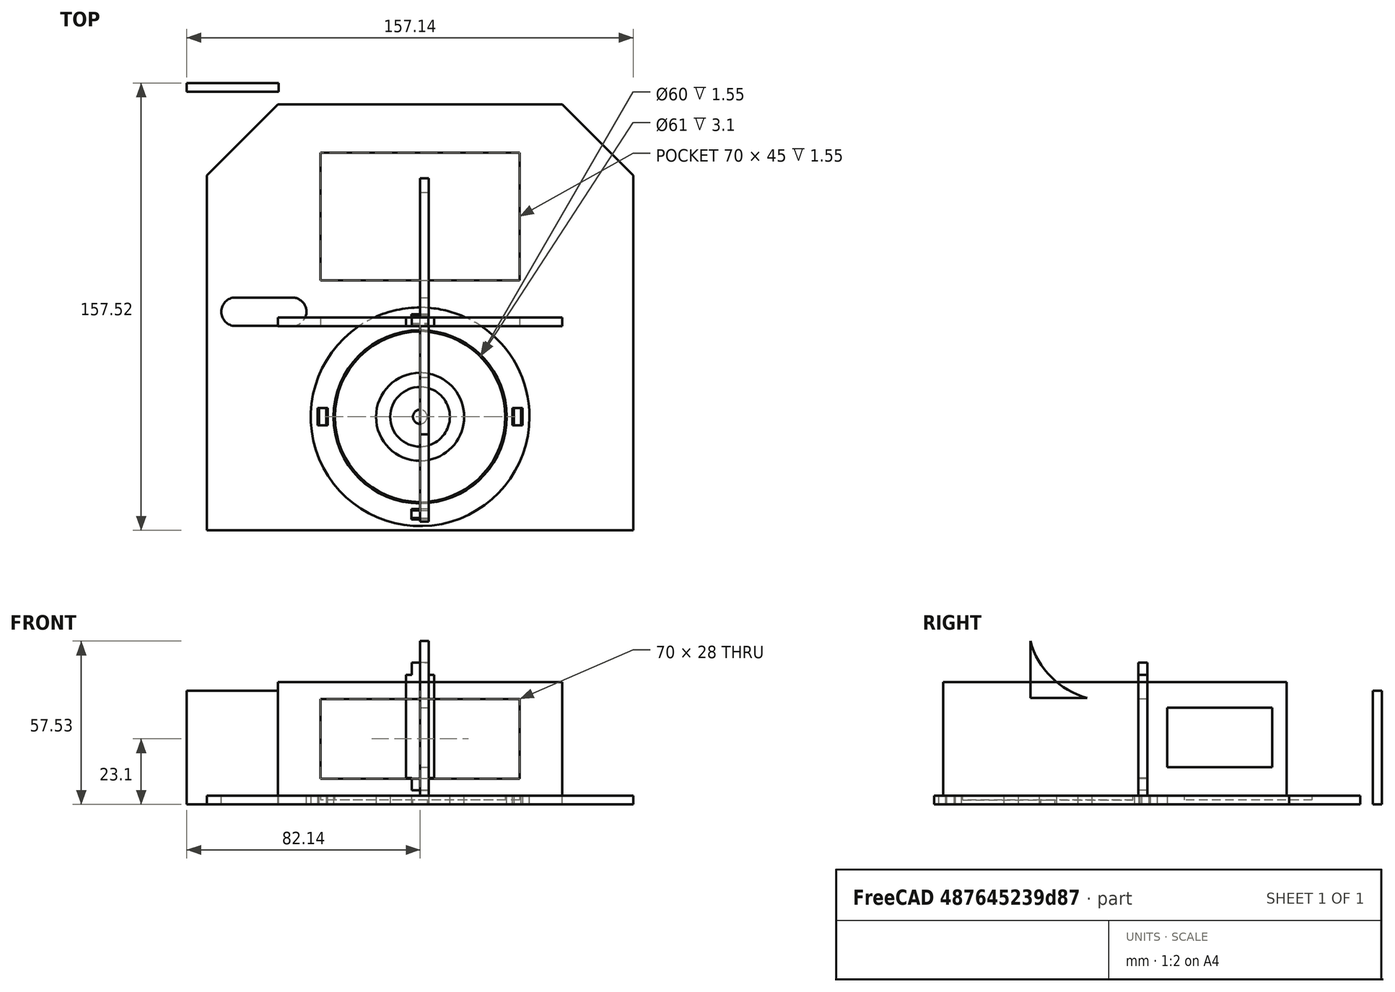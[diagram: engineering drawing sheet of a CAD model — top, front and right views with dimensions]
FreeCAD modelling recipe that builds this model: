
FCSTD DOCUMENT  (FreeCAD 1.0R39109 (Git))
Label: Vehicle_project_3
License: All rights reserved
LicenseURL: https://en.wikipedia.org/wiki/All_rights_reserved
objects: Sketcher::SketchObject×29, PartDesign::Pocket×17, App::Link×15, App::FeaturePython×15, PartDesign::Pad×12, PartDesign::Body×12, Part::Part2DObjectPython×12, Part::FeaturePython×3, PartDesign::Fillet×2, PartDesign::Mirrored×2, App::DocumentObjectGroup×2, App::VarSet×1, Part::Plane×1, App::Part×1, Assembly::JointGroup×1, Assembly::AssemblyObject×1
note: 183 computed .brp shape members not serialized (recipe doc carries the construction recipe); baked Part::Feature solids carry a one-line shape summary decoded from their .brp

FEATURE [App::VarSet] VarSet  label="dimensions"
  base_height = 40
  base_length = 150
  base_short_side = 25
  base_width = 150
  board_length = 50
  board_width = 80
  bridge_side = 45
  hole_margin = 1
  material_thickness = 3.1
  raspberry_length = 61
  raspberry_width = 89
FEATURE [Sketcher::SketchObject] Sketch
  ArcFitTolerance = 1e-06
  AttachmentSupport = -> [XY_Plane]
  FullyConstrained = true
  MakeInternals = false
  MapMode = 5
  expr: Constraints[11] = <<dimensions>>.base_width
  expr: Constraints[12] = <<dimensions>>.base_length
  expr: Constraints[14] = <<dimensions>>.base_length / 2
  expr: Constraints[15] = <<dimensions>>.base_short_side
  expr: Constraints[16] = <<dimensions>>.base_short_side
  sketch-geometry (6):
    g0: LineSegment StartX=-75 StartY=50 StartZ=0 EndX=-75 EndY=-75 EndZ=0
    g1: LineSegment StartX=-75 StartY=-75 StartZ=0 EndX=75 EndY=-75 EndZ=0
    g2: LineSegment StartX=75 StartY=-75 StartZ=0 EndX=75 EndY=50 EndZ=0
    g3: LineSegment StartX=75 StartY=50 StartZ=0 EndX=50 EndY=75 EndZ=0
    g4: LineSegment StartX=50 StartY=75 StartZ=0 EndX=-50 EndY=75 EndZ=0
    g5: LineSegment StartX=-50 StartY=75 StartZ=0 EndX=-75 EndY=50 EndZ=0
  constraints (17):
    c: Vertical(g0)
    c: Coincident(g0,g1)
    c: Horizontal(g1)
    c: Coincident(g1,g2)
    c: Vertical(g2)
    c: Coincident(g2,g3)
    c: Coincident(g3,g4)
    c: Horizontal(g4)
    c: Coincident(g4,g5)
    c: Coincident(g5,g0)
    c: Equal(g5,g3)
    c: DistanceX(g1,g1) = 150
    c: Distance(g1,g4) = 150
    c: Symmetric(g0,g2,g-2)
    c: Distance(g-1,g1) = 75
    c: DistanceY(g0,g4) = 25
    c: DistanceX(g0,g4) = 25
FEATURE [PartDesign::Pad] Pad
  Direction = (0,0,1)
  Length = 3.1
  Length2 = 10
  Profile = -> Sketch
  ReferenceAxis = -> Sketch [N_Axis]
  Refine = true
  Suppressed = false
  Type = 0
  expr: Length = <<dimensions>>.material_thickness
FEATURE [Sketcher::SketchObject] Sketch001
  ArcFitTolerance = 1e-06
  AttachmentSupport = -> [Pad]
  ExternalGeometry = -> [Pad]
  FullyConstrained = true
  MakeInternals = false
  MapMode = 5
  Placement = pos=(0,0,3.1) rot=(0,0,1;0rad)
  expr: Constraints[10] = <<dimensions>>.material_thickness + <<dimensions>>.hole_margin
  expr: Constraints[11] = <<dimensions>>.material_thickness + <<dimensions>>.hole_margin
  expr: Constraints[8] = <<dimensions>>.raspberry_width
  expr: Constraints[9] = <<dimensions>>.raspberry_length
  sketch-geometry (4):
    g0: LineSegment StartX=-70.9 StartY=-9.9 StartZ=0 EndX=-70.9 EndY=-70.9 EndZ=0
    g1: LineSegment StartX=-70.9 StartY=-70.9 StartZ=0 EndX=18.1 EndY=-70.9 EndZ=0
    g2: LineSegment StartX=18.1 StartY=-70.9 StartZ=0 EndX=18.1 EndY=-9.9 EndZ=0
    g3: LineSegment StartX=18.1 StartY=-9.9 StartZ=0 EndX=-70.9 EndY=-9.9 EndZ=0
  constraints (12):
    c: Vertical(g0)
    c: Coincident(g0,g1)
    c: Coincident(g1,g2)
    c: Coincident(g2,g3)
    c: Coincident(g3,g0)
    c: Horizontal(g0,g2)
    c: Horizontal(g1,g0)
    c: Vertical(g2)
    c: DistanceX(g3,g3) = 89
    c: DistanceY(g2,g2) = 61
    c: Distance(g-3,g0) = 4.1
    c: Distance(g1,g-4) = 4.1
FEATURE [PartDesign::Pocket] Pocket
  BaseFeature = -> Pad
  Direction = (0,0,-1)
  Length = 1.55
  Length2 = 5
  Profile = -> Sketch001
  ReferenceAxis = -> Sketch001 [N_Axis]
  Refine = true
  Suppressed = false
  Type = 0
  expr: Length = <<dimensions>>.material_thickness / 2
FEATURE [Sketcher::SketchObject] Sketch002
  ArcFitTolerance = 1e-06
  AttachmentSupport = -> [Pocket]
  ExternalGeometry = -> [Pocket]
  FullyConstrained = true
  MakeInternals = false
  MapMode = 5
  Placement = pos=(0,0,3.1) rot=(0,0,1;0rad)
  sketch-geometry (4):
    g0: LineSegment StartX=-70.9 StartY=46.8875 StartZ=0 EndX=-70.9 EndY=-3.11249 EndZ=0
    g1: LineSegment StartX=-70.9 StartY=-3.11249 StartZ=0 EndX=9.1 EndY=-3.11249 EndZ=0
    g2: LineSegment StartX=9.1 StartY=-3.11249 StartZ=0 EndX=9.1 EndY=46.8875 EndZ=0
    g3: LineSegment StartX=9.1 StartY=46.8875 StartZ=0 EndX=-70.9 EndY=46.8875 EndZ=0
  constraints (12):
    c: Coincident(g0,g1)
    c: Coincident(g1,g2)
    c: Coincident(g2,g3)
    c: Coincident(g3,g0)
    c: Horizontal(g3)
    c: Horizontal(g1)
    c: Vertical(g2)
    c: Vertical(g0)
    c: DistanceX(g3,g3) = 80  '=di'
    c: DistanceY(g0,g0) = 50
    c: Vertical(g0,g-4)
    c: Distance(g0,g-6) = 5.1
FEATURE [PartDesign::Pocket] Pocket001
  BaseFeature = -> Pocket
  Direction = (0,0,-1)
  Length = 1.55
  Length2 = 5
  Profile = -> Sketch002
  ReferenceAxis = -> Sketch002 [N_Axis]
  Refine = true
  Suppressed = false
  Type = 0
  expr: Length = <<dimensions>>.material_thickness / 2
FEATURE [Sketcher::SketchObject] Sketch003
  ArcFitTolerance = 1e-06
  AttachmentSupport = -> [Pocket001]
  ExternalGeometry = -> [Pocket001]
  FullyConstrained = true
  MakeInternals = false
  MapMode = 5
  Placement = pos=(0,0,3.1) rot=(0,0,1;0rad)
  expr: Constraints[9] = <<dimensions>>.material_thickness + 3 mm
  sketch-geometry (4):
    g0: LineSegment StartX=45 StartY=-61.9 StartZ=0 EndX=45 EndY=-68.9 EndZ=0
    g1: LineSegment StartX=45 StartY=-68.9 StartZ=0 EndX=60 EndY=-68.9 EndZ=0
    g2: LineSegment StartX=60 StartY=-68.9 StartZ=0 EndX=60 EndY=-61.9 EndZ=0
    g3: LineSegment StartX=60 StartY=-61.9 StartZ=0 EndX=45 EndY=-61.9 EndZ=0
  constraints (12):
    c: Coincident(g0,g1)
    c: Coincident(g1,g2)
    c: Coincident(g2,g3)
    c: Coincident(g3,g0)
    c: Horizontal(g3)
    c: Horizontal(g1)
    c: Vertical(g0)
    c: Vertical(g2)
    c: Distance(g-3,g2) = 15
    c: Distance(g-4,g1) = 6.1
    c: DistanceY(g2,g2) = 7
    c: DistanceX(g3,g3) = 15
FEATURE [PartDesign::Pocket] Pocket002
  BaseFeature = -> Pocket001
  Direction = (0,0,-1)
  Length = 5
  Length2 = 5
  Profile = -> Sketch003
  ReferenceAxis = -> Sketch003 [N_Axis]
  Refine = true
  Suppressed = false
  Type = 1
FEATURE [PartDesign::Fillet] Fillet
  Base = -> Pocket002 [Edge36,Edge38,Edge35,Edge37]
  BaseFeature = -> Pocket002
  Radius = 3
  Refine = true
  SupportTransform = false
  Suppressed = false
  UseAllEdges = false
FEATURE [Sketcher::SketchObject] Sketch004
  ArcFitTolerance = 1e-06
  AttachmentSupport = -> [Fillet]
  ExternalGeometry = -> [Fillet]
  FullyConstrained = true
  MakeInternals = false
  MapMode = 5
  Placement = pos=(0,0,3.1) rot=(0,0,1;0rad)
  expr: Constraints[8] = <<dimensions>>.bridge_side
  expr: Constraints[9] = <<dimensions>>.bridge_side
  sketch-geometry (4):
    g0: LineSegment StartX=19.1 StartY=46.8875 StartZ=0 EndX=19.1 EndY=1.88751 EndZ=0
    g1: LineSegment StartX=19.1 StartY=1.88751 StartZ=0 EndX=64.1 EndY=1.88751 EndZ=0
    g2: LineSegment StartX=64.1 StartY=1.88751 StartZ=0 EndX=64.1 EndY=46.8875 EndZ=0
    g3: LineSegment StartX=64.1 StartY=46.8875 StartZ=0 EndX=19.1 EndY=46.8875 EndZ=0
  constraints (12):
    c: Vertical(g0)
    c: Coincident(g0,g1)
    c: Coincident(g1,g2)
    c: Coincident(g2,g3)
    c: Coincident(g3,g0)
    c: Horizontal(g3)
    c: Vertical(g2)
    c: Horizontal(g1)
    c: DistanceY(g2,g2) = 45
    c: DistanceX(g3,g3) = 45
    c: Distance(g-3,g0) = 10
    c: Horizontal(g-3,g0)
FEATURE [PartDesign::Pocket] Pocket003
  BaseFeature = -> Fillet
  Direction = (0,0,-1)
  Length = 1.55
  Length2 = 5
  Profile = -> Sketch004
  ReferenceAxis = -> Sketch004 [N_Axis]
  Refine = true
  Suppressed = false
  Type = 0
  expr: Length = <<dimensions>>.material_thickness / 2
FEATURE [Sketcher::SketchObject] Sketch005
  ArcFitTolerance = 1e-06
  AttachmentSupport = -> [XZ_Plane001]
  FullyConstrained = true
  MakeInternals = false
  MapMode = 5
  Placement = pos=(0,0,0) rot=(1,0,0;1.5708rad)
  expr: Constraints[10] = <<dimensions>>.material_thickness
  expr: Constraints[7] = <<dimensions>>.base_width
  expr: Constraints[8] = <<dimensions>>.base_height
  sketch-geometry (4):
    g0: LineSegment StartX=-75 StartY=43.1 StartZ=0 EndX=-75 EndY=3.1 EndZ=0
    g1: LineSegment StartX=-75 StartY=3.1 StartZ=0 EndX=75 EndY=3.1 EndZ=0
    g2: LineSegment StartX=75 StartY=3.1 StartZ=0 EndX=75 EndY=43.1 EndZ=0
    g3: LineSegment StartX=75 StartY=43.1 StartZ=0 EndX=-75 EndY=43.1 EndZ=0
  constraints (11):
    c: Vertical(g0)
    c: Coincident(g0,g1)
    c: Horizontal(g1)
    c: Coincident(g1,g2)
    c: Coincident(g2,g3)
    c: Coincident(g3,g0)
    c: Vertical(g2)
    c: DistanceX(g3,g3) = 150
    c: DistanceY(g2,g2) = 40
    c: Symmetric(g0,g2,g-2)
    c: Distance(g-1,g1) = 3.1
FEATURE [PartDesign::Pad] Pad001
  Direction = (0,-1,2e-16)
  Length = 3.1
  Length2 = 10
  Placement = pos=(0,0,0) rot=(1,0,0;1.5708rad)
  Profile = -> Sketch005
  ReferenceAxis = -> Sketch005 [N_Axis]
  Refine = true
  Suppressed = false
  Type = 0
  expr: Length = <<dimensions>>.material_thickness
FEATURE [Sketcher::SketchObject] Sketch006
  ArcFitTolerance = 1e-06
  AttachmentSupport = -> [Pad001]
  ExternalGeometry = -> [Pad001]
  FullyConstrained = true
  MakeInternals = false
  MapMode = 5
  Placement = pos=(0,-3.1,0) rot=(1,0,0;1.5708rad)
  expr: Constraints[8] = <<dimensions>>.material_thickness + 5 mm
  sketch-geometry (4):
    g0: LineSegment StartX=-66.9 StartY=18.1 StartZ=0 EndX=-66.9 EndY=6.1 EndZ=0
    g1: LineSegment StartX=-66.9 StartY=6.1 StartZ=0 EndX=-51.9 EndY=6.1 EndZ=0
    g2: LineSegment StartX=-51.9 StartY=6.1 StartZ=0 EndX=-51.9 EndY=18.1 EndZ=0
    g3: LineSegment StartX=-51.9 StartY=18.1 StartZ=0 EndX=-66.9 EndY=18.1 EndZ=0
  constraints (12):
    c: Coincident(g0,g1)
    c: Horizontal(g1)
    c: Coincident(g1,g2)
    c: Coincident(g2,g3)
    c: Coincident(g3,g0)
    c: Horizontal(g3)
    c: Vertical(g2)
    c: Vertical(g0)
    c: Distance(g-3,g0) = 8.1
    c: Distance(g-4,g1) = 3
    c: DistanceY(g0,g0) = 12
    c: DistanceX(g1,g1) = 15
FEATURE [PartDesign::Pocket] Pocket004
  BaseFeature = -> Pad001
  Direction = (0,1,-2e-16)
  Length = 5
  Length2 = 5
  Placement = pos=(0,0,0) rot=(1,0,0;1.5708rad)
  Profile = -> Sketch006
  ReferenceAxis = -> Sketch006 [N_Axis]
  Refine = true
  Suppressed = false
  Type = 1
FEATURE [PartDesign::Fillet] Fillet001
  Base = -> Pocket004 [Edge23,Edge22,Edge21,Edge24]
  BaseFeature = -> Pocket004
  Placement = pos=(0,0,0) rot=(1,0,0;1.5708rad)
  Radius = 2
  Refine = true
  SupportTransform = false
  Suppressed = false
  UseAllEdges = false
FEATURE [PartDesign::Body] Body001  label="back_side"
  AllowCompound = false
  Group = -> [Sketch005,Pad001,Sketch006,Pocket004,Fillet001]
  Origin = -> Origin001
  Tip = -> Fillet001
FEATURE [Sketcher::SketchObject] Sketch007
  ArcFitTolerance = 1e-06
  AttachmentSupport = -> [YZ_Plane002]
  FullyConstrained = true
  MakeInternals = false
  MapMode = 5
  Placement = pos=(0,0,0) rot=(0.57735,0.57735,0.57735;2.0944rad)
  expr: Constraints[10] = <<dimensions>>.base_length / 2 - <<dimensions>>.material_thickness
  expr: Constraints[11] = <<dimensions>>.material_thickness
  expr: Constraints[8] = <<dimensions>>.base_height
  expr: Constraints[9] = <<dimensions>>.base_length - <<dimensions>>.material_thickness - 26 mm
  sketch-geometry (4):
    g0: LineSegment StartX=-71.9 StartY=43.1 StartZ=0 EndX=-71.9 EndY=3.1 EndZ=0
    g1: LineSegment StartX=-71.9 StartY=3.1 StartZ=0 EndX=49 EndY=3.1 EndZ=0
    g2: LineSegment StartX=-71.9 StartY=43.1 StartZ=0 EndX=49 EndY=43.1 EndZ=0
    g3: LineSegment StartX=49 StartY=43.1 StartZ=0 EndX=49 EndY=3.1 EndZ=0
  constraints (12):
    c: Coincident(g0,g1)
    c: Horizontal(g1)
    c: Coincident(g0,g2)
    c: Coincident(g2,g3)
    c: Coincident(g3,g1)
    c: Vertical(g3)
    c: Horizontal(g2)
    c: Vertical(g0)
    c: DistanceY(g0,g0) = 40
    c: DistanceX(g1,g1) = 120.9
    c: Distance(g-2,g0) = 71.9
    c: Distance(g-1,g1) = 3.1
FEATURE [PartDesign::Pad] Pad002
  Direction = (1,0,0)
  Length = 3.1
  Length2 = 10
  Placement = pos=(0,0,0) rot=(1,1,1;2.0944rad)
  Profile = -> Sketch007
  ReferenceAxis = -> Sketch007 [N_Axis]
  Refine = true
  Suppressed = false
  Type = 0
  expr: Length = <<dimensions>>.material_thickness
FEATURE [PartDesign::Body] Body002  label="right_side"
  AllowCompound = false
  Group = -> [Sketch007,Pad002]
  Origin = -> Origin002
  Tip = -> Pad002
FEATURE [Sketcher::SketchObject] Sketch008
  ArcFitTolerance = 1e-06
  AttachmentSupport = -> [YZ_Plane003]
  FullyConstrained = true
  MakeInternals = false
  MapMode = 5
  Placement = pos=(0,0,0) rot=(0.57735,0.57735,0.57735;2.0944rad)
  sketch-geometry (4):
    g0: LineSegment StartX=-71.9 StartY=43.1 StartZ=0 EndX=-71.9 EndY=3.1 EndZ=0
    g1: LineSegment StartX=-71.9 StartY=3.1 StartZ=0 EndX=49 EndY=3.1 EndZ=0
    g2: LineSegment StartX=-71.9 StartY=43.1 StartZ=0 EndX=49 EndY=43.1 EndZ=0
    g3: LineSegment StartX=49 StartY=43.1 StartZ=0 EndX=49 EndY=3.1 EndZ=0
  constraints (12):
    c: Coincident(g0,g1)
    c: Horizontal(g1)
    c: Coincident(g0,g2)
    c: Coincident(g2,g3)
    c: Coincident(g3,g1)
    c: Vertical(g3)
    c: Horizontal(g2)
    c: Vertical(g0)
    c: DistanceY(g0,g0) = 40
    c: DistanceX(g1,g1) = 120.9
    c: Distance(g-2,g0) = 71.9
    c: Distance(g-1,g1) = 3.1
FEATURE [PartDesign::Pad] Pad003
  Direction = (1,0,0)
  Length = 3.1
  Length2 = 10
  Placement = pos=(0,0,0) rot=(1,1,1;2.0944rad)
  Profile = -> Sketch008
  ReferenceAxis = -> Sketch008 [N_Axis]
  Refine = true
  Suppressed = false
  Type = 0
  expr: Length = <<dimensions>>.material_thickness
FEATURE [Sketcher::SketchObject] Sketch009
  ArcFitTolerance = 1e-06
  AttachmentSupport = -> [Pad003]
  ExternalGeometry = -> [Pad003]
  FullyConstrained = true
  MakeInternals = false
  MapMode = 5
  Placement = pos=(0,0,0) rot=(0.57735,0.57735,-0.57735;4.18879rad)
  sketch-geometry (4):
    g0: LineSegment StartX=44 StartY=-34.1 StartZ=0 EndX=44 EndY=-13.1 EndZ=0
    g1: LineSegment StartX=44 StartY=-13.1 StartZ=0 EndX=7 EndY=-13.1 EndZ=0
    g2: LineSegment StartX=7 StartY=-13.1 StartZ=0 EndX=7 EndY=-34.1 EndZ=0
    g3: LineSegment StartX=7 StartY=-34.1 StartZ=0 EndX=44 EndY=-34.1 EndZ=0
  constraints (12):
    c: Coincident(g0,g1)
    c: Horizontal(g1)
    c: Coincident(g1,g2)
    c: Coincident(g2,g3)
    c: Coincident(g3,g0)
    c: Horizontal(g3)
    c: Vertical(g0)
    c: Vertical(g2)
    c: Distance(g-4,g0) = 5
    c: Distance(g-3,g3) = 9
    c: DistanceY(g0,g0) = 21
    c: DistanceX(g1,g1) = 37
FEATURE [PartDesign::Pocket] Pocket005
  BaseFeature = -> Pad003
  Direction = (1,0,0)
  Length = 5
  Length2 = 5
  Placement = pos=(0,0,0) rot=(1,1,1;2.0944rad)
  Profile = -> Sketch009
  ReferenceAxis = -> Sketch009 [N_Axis]
  Refine = true
  Suppressed = false
  Type = 1
FEATURE [PartDesign::Body] Body003  label="left_side"
  AllowCompound = false
  Group = -> [Sketch008,Pad003,Sketch009,Pocket005]
  Origin = -> Origin003
  Tip = -> Pocket005
FEATURE [Sketcher::SketchObject] Sketch010
  ArcFitTolerance = 1e-06
  AttachmentSupport = -> [XY_Plane004]
  FullyConstrained = false
  MakeInternals = false
  MapMode = 5
  expr: Constraints[8] = sqrt(1250) - 3
  expr: Constraints[9] = <<dimensions>>.material_thickness
  sketch-geometry (4):
    g0: LineSegment StartX=-82.1409 StartY=82.5247 StartZ=0 EndX=-49.7856 EndY=82.5247 EndZ=0
    g1: LineSegment StartX=-49.7856 StartY=82.5247 StartZ=0 EndX=-49.7856 EndY=79.4247 EndZ=0
    g2: LineSegment StartX=-49.7856 StartY=79.4247 StartZ=0 EndX=-82.1409 EndY=79.4247 EndZ=0
    g3: LineSegment StartX=-82.1409 StartY=79.4247 StartZ=0 EndX=-82.1409 EndY=82.5247 EndZ=0
  constraints (10):
    c: Horizontal(g0)
    c: Coincident(g0,g1)
    c: Coincident(g1,g2)
    c: Horizontal(g2)
    c: Coincident(g2,g3)
    c: Coincident(g3,g0)
    c: Vertical(g3)
    c: Vertical(g1)
    c: DistanceX(g0,g0) = 32.3553
    c: DistanceY(g1,g1) = 3.1
FEATURE [PartDesign::Pad] Pad004
  Direction = (0,0,1)
  Length = 40
  Length2 = 10
  Profile = -> Sketch010
  ReferenceAxis = -> Sketch010 [N_Axis]
  Refine = true
  Suppressed = false
  Type = 0
  expr: Length = <<dimensions>>.base_height
FEATURE [PartDesign::Body] Body004  label="front_angle_side"
  AllowCompound = false
  Group = -> [Sketch010,Pad004]
  Origin = -> Origin004
  Tip = -> Pad004
FEATURE [Sketcher::SketchObject] Sketch011
  ArcFitTolerance = 1e-06
  AttachmentSupport = -> [XZ_Plane005]
  FullyConstrained = true
  MakeInternals = false
  MapMode = 5
  Placement = pos=(0,0,0) rot=(1,0,0;1.5708rad)
  expr: Constraints[15] = <<dimensions>>.base_width / 2 - 25 mm
  expr: Constraints[18] = <<dimensions>>.material_thickness
  expr: Constraints[23] = <<dimensions>>.base_height
  sketch-geometry (8):
    g0: LineSegment StartX=0 StartY=43.1 StartZ=0 EndX=0 EndY=37.1 EndZ=0
    g1: LineSegment StartX=-35 StartY=37.1 StartZ=0 EndX=-35 EndY=9.1 EndZ=0
    g2: LineSegment StartX=-35 StartY=9.1 StartZ=0 EndX=0 EndY=9.1 EndZ=0
    g3: LineSegment StartX=0 StartY=9.1 StartZ=0 EndX=0 EndY=3.1 EndZ=0
    g4: LineSegment StartX=0 StartY=3.1 StartZ=0 EndX=-50 EndY=3.1 EndZ=0
    g5: LineSegment StartX=-50 StartY=3.1 StartZ=0 EndX=-50 EndY=43.1 EndZ=0
    g6: LineSegment StartX=-50 StartY=43.1 StartZ=0 EndX=0 EndY=43.1 EndZ=0
    g7: LineSegment StartX=0 StartY=37.1 StartZ=0 EndX=-35 EndY=37.1 EndZ=0
  constraints (24):
    c: PointOnObject(g0,g-2)
    c: PointOnObject(g0,g-2)
    c: Vertical(g1)
    c: Coincident(g1,g2)
    c: PointOnObject(g2,g-2)
    c: Horizontal(g2)
    c: Coincident(g2,g3)
    c: PointOnObject(g3,g-2)
    c: Coincident(g3,g4)
    c: Horizontal(g4)
    c: Coincident(g4,g5)
    c: Vertical(g5)
    c: Coincident(g5,g6)
    c: Coincident(g6,g0)
    c: Horizontal(g6)
    c: DistanceX(g4,g4) = 50
    c: Distance(g4,g2) = 6
    c: Distance(g5,g1) = 15
    c: Distance(g-1,g4) = 3.1
    c: Coincident(g0,g7)
    c: Coincident(g7,g1)
    c: Horizontal(g7)
    c: Distance(g6,g7) = 6
    c: DistanceY(g5,g5) = 40
FEATURE [PartDesign::Pad] Pad005
  Direction = (0,-1,2e-16)
  Length = 3.1
  Length2 = 10
  Placement = pos=(0,0,0) rot=(1,0,0;1.5708rad)
  Profile = -> Sketch011
  ReferenceAxis = -> Sketch011 [N_Axis]
  Refine = true
  Suppressed = false
  Type = 0
  expr: Length = <<dimensions>>.material_thickness
FEATURE [PartDesign::Mirrored] Mirrored
  BaseFeature = -> Pad005
  MirrorPlane = -> YZ_Plane005
  Placement = pos=(0,0,0) rot=(1,0,0;1.5708rad)
  Refine = true
  Suppressed = false
  TransformMode = 1
FEATURE [PartDesign::Body] Body005  label="front_side"
  AllowCompound = false
  Group = -> [Sketch011,Pad005,Mirrored]
  Origin = -> Origin005
  Tip = -> Mirrored
FEATURE [App::Link] base  label="base001"
  LinkedObject = -> Body
FEATURE [App::FeaturePython] GroundedJoint  # Assembly grounded joint (typed FeaturePython)
  ObjectToGround = -> base
FEATURE [App::Link] back_side  label="back_side001"
  LinkPlacement = pos=(-3e-15,-71.9,-1e-15) rot=(0,0,1;0rad)
  LinkedObject = -> Body001
  Placement = pos=(-3e-15,-71.9,-1e-15) rot=(0,0,1;0rad)
FEATURE [App::FeaturePython] Joint  label="Fixed"  # Assembly joint (typed FeaturePython)
  Activated = true
  AngleMax = 0
  AngleMin = 0
  Detach1 = false
  Detach2 = false
  Distance = 0
  Distance2 = 0
  EnableAngleMax = false
  EnableAngleMin = false
  EnableLengthMax = false
  EnableLengthMin = false
  JointType = 0 (Fixed)
  LengthMax = 0
  LengthMin = 0
  Placement1 = pos=(3e-15,-3.1,3.1) rot=(0.707107,0,0.707107;3.14159rad)
  Placement2 = pos=(0,-75,3.1) rot=(0.707107,0,0.707107;3.14159rad)
  Reference1 = -> Assembly [back_side.Edge35,back_side.Edge35]
  Reference2 = -> Assembly [base.Edge37,base.Edge37]
FEATURE [App::Link] left_side  label="left_side001"
  LinkPlacement = pos=(-75,-3.57e-14,3.6e-14) rot=(0,0,1;0rad)
  LinkedObject = -> Body003
  Placement = pos=(-75,-3.57e-14,3.6e-14) rot=(0,0,1;0rad)
FEATURE [App::Link] right_side  label="right_side001"
  LinkPlacement = pos=(71.9,-1.35e-14,1.91e-14) rot=(0,0,1;0rad)
  LinkedObject = -> Body002
  Placement = pos=(71.9,-1.35e-14,1.91e-14) rot=(0,0,1;0rad)
FEATURE [App::FeaturePython] Joint001  label="Fixed001"  # Assembly joint (typed FeaturePython)
  Activated = true
  AngleMax = 0
  AngleMin = 0
  Detach1 = false
  Detach2 = false
  Distance = 0
  Distance2 = 0
  EnableAngleMax = false
  EnableAngleMin = false
  EnableLengthMax = false
  EnableLengthMin = false
  JointType = 0 (Fixed)
  LengthMax = 0
  LengthMin = 0
  Offset2 = pos=(0,0,1) rot=(0,0,1;3.14159rad)
  Placement1 = pos=(0,49,3.1) rot=(0.57735,0.57735,0.57735;4.18879rad)
  Placement2 = pos=(-75,49,3.1) rot=(-0.57735,0.57735,-0.57735;4.18879rad)
  Reference1 = -> Assembly [left_side.Edge9,left_side.Vertex7]
  Reference2 = -> Assembly [base.Edge33,base.Vertex23]
FEATURE [App::FeaturePython] Joint002  label="Fixed002"  # Assembly joint (typed FeaturePython)
  Activated = true
  AngleMax = 0
  AngleMin = 0
  Detach1 = false
  Detach2 = false
  Distance = 0
  Distance2 = 0
  EnableAngleMax = false
  EnableAngleMin = false
  EnableLengthMax = false
  EnableLengthMin = false
  JointType = 0 (Fixed)
  LengthMax = 0
  LengthMin = 0
  Offset2 = pos=(0,0,-1) rot=(0,0,1;0rad)
  Placement1 = pos=(3.1,49,3.1) rot=(0.57735,0.57735,0.57735;4.18879rad)
  Placement2 = pos=(75,49,3.1) rot=(0.57735,0.57735,0.57735;4.18879rad)
  Reference1 = -> Assembly [right_side.Edge7,right_side.Vertex6]
  Reference2 = -> Assembly [base.Edge41,base.Vertex28]
FEATURE [App::Link] front_angle_side  label="front_angle_side001"
  LinkPlacement = pos=(50.7893,-42.4969,3.1) rot=(0,0,-1;0.785398rad)
  LinkedObject = -> Body004
  Placement = pos=(50.7893,-42.4969,3.1) rot=(0,0,-1;0.785398rad)
FEATURE [App::Link] front_angle_side001  label="front_angle_side002"
  LinkPlacement = pos=(43.0783,51.3707,3.1) rot=(0,0,1;0.785398rad)
  LinkedObject = -> Body004
  Placement = pos=(43.0783,51.3707,3.1) rot=(0,0,1;0.785398rad)
FEATURE [App::FeaturePython] Joint003  label="Fixed003"  # Assembly joint (typed FeaturePython)
  Activated = true
  AngleMax = 0
  AngleMin = 0
  Detach1 = false
  Detach2 = false
  Distance = 0
  Distance2 = 0
  EnableAngleMax = false
  EnableAngleMin = false
  EnableLengthMax = false
  EnableLengthMin = false
  JointType = 0 (Fixed)
  LengthMax = 0
  LengthMin = 0
  Offset2 = pos=(0,0,0) rot=(0,0,-1;1.5708rad)
  Placement1 = pos=(-65.9632,82.5247,0) rot=(0.707107,0,0.707107;3.14159rad)
  Placement2 = pos=(62.5,62.5,3.1) rot=(-0.357407,-0.862856,-0.357407;1.71777rad)
  Reference1 = -> Assembly [front_angle_side.Edge3,front_angle_side.Edge3]
  Reference2 = -> Assembly [base.Edge42,base.Edge42]
FEATURE [App::FeaturePython] Joint004  label="Fixed004"  # Assembly joint (typed FeaturePython)
  Activated = true
  AngleMax = 0
  AngleMin = 0
  Detach1 = false
  Detach2 = false
  Distance = 0
  Distance2 = 0
  EnableAngleMax = false
  EnableAngleMin = false
  EnableLengthMax = false
  EnableLengthMin = false
  JointType = 0 (Fixed)
  LengthMax = 0
  LengthMin = 0
  Offset2 = pos=(0,0,-17) rot=(0,0,-1;1.5708rad)
  Placement1 = pos=(-49.7856,82.5247,0) rot=(0.707107,0,0.707107;3.14159rad)
  Placement2 = pos=(-50.4792,74.5208,3.1) rot=(0.357407,-0.862856,0.357407;1.71777rad)
  Reference1 = -> Assembly [front_angle_side001.Edge3,front_angle_side001.Vertex3]
  Reference2 = -> Assembly [base.Edge35,base.Edge35]
FEATURE [App::Link] front_side  label="front_side001"
  LinkPlacement = pos=(2.7e-15,75,-5.4e-15) rot=(0,0,1;0rad)
  LinkedObject = -> Body005
  Placement = pos=(2.7e-15,75,-5.4e-15) rot=(0,0,1;0rad)
FEATURE [App::FeaturePython] Joint005  label="Fixed005"  # Assembly joint (typed FeaturePython)
  Activated = true
  AngleMax = 0
  AngleMin = 0
  Detach1 = false
  Detach2 = false
  Distance = 0
  Distance2 = 0
  EnableAngleMax = false
  EnableAngleMin = false
  EnableLengthMax = false
  EnableLengthMin = false
  JointType = 0 (Fixed)
  LengthMax = 0
  LengthMin = 0
  Offset2 = pos=(0,0,0) rot=(0,0,1;3.14159rad)
  Placement1 = pos=(-2.7e-15,0,3.1) rot=(0.707107,0,0.707107;3.14159rad)
  Placement2 = pos=(0,75,3.1) rot=(0,1,0;4.71239rad)
  Reference1 = -> Assembly [front_side.Edge7,front_side.Edge7]
  Reference2 = -> Assembly [base.Edge39,base.Edge39]
FEATURE [Sketcher::SketchObject] Sketch012
  ArcFitTolerance = 1e-06
  AttachmentSupport = -> [XY_Plane007]
  FullyConstrained = true
  MakeInternals = false
  MapMode = 5
  expr: Constraints[11] = <<dimensions>>.base_width
  expr: Constraints[12] = <<dimensions>>.base_length
  expr: Constraints[14] = <<dimensions>>.base_length / 2
  sketch-geometry (6):
    g0: LineSegment StartX=-75 StartY=50 StartZ=0 EndX=-75 EndY=-75 EndZ=0
    g1: LineSegment StartX=-75 StartY=-75 StartZ=0 EndX=75 EndY=-75 EndZ=0
    g2: LineSegment StartX=75 StartY=-75 StartZ=0 EndX=75 EndY=50 EndZ=0
    g3: LineSegment StartX=75 StartY=50 StartZ=0 EndX=50 EndY=75 EndZ=0
    g4: LineSegment StartX=50 StartY=75 StartZ=0 EndX=-50 EndY=75 EndZ=0
    g5: LineSegment StartX=-50 StartY=75 StartZ=0 EndX=-75 EndY=50 EndZ=0
  constraints (17):
    c: Vertical(g0)
    c: Coincident(g0,g1)
    c: Horizontal(g1)
    c: Coincident(g1,g2)
    c: Vertical(g2)
    c: Coincident(g2,g3)
    c: Coincident(g3,g4)
    c: Horizontal(g4)
    c: Coincident(g4,g5)
    c: Coincident(g5,g0)
    c: Equal(g5,g3)
    c: DistanceX(g1,g1) = 150
    c: Distance(g1,g4) = 150
    c: Symmetric(g0,g2,g-2)
    c: Distance(g-1,g1) = 75
    c: DistanceY(g0,g4) = 25
    c: DistanceX(g0,g4) = 25
FEATURE [PartDesign::Pad] Pad006
  Direction = (0,0,1)
  Length = 3.1
  Length2 = 10
  Profile = -> Sketch012
  ReferenceAxis = -> Sketch012 [N_Axis]
  Refine = true
  Suppressed = false
  Type = 0
  expr: Length = <<dimensions>>.material_thickness
FEATURE [App::FeaturePython] Joint007  label="Fixed006"  # Assembly joint (typed FeaturePython)
  Activated = true
  AngleMax = 0
  AngleMin = 0
  Detach1 = false
  Detach2 = false
  Distance = 0
  Distance2 = 0
  EnableAngleMax = false
  EnableAngleMin = false
  EnableLengthMax = false
  EnableLengthMin = false
  JointType = 0 (Fixed)
  LengthMax = 0
  LengthMin = 0
  Offset2 = pos=(0,0,-3) rot=(0,0,1;3.14159rad)
  Placement1 = pos=(-75,-75,0) rot=(-0.57735,-0.57735,0.57735;4.18879rad)
  Placement2 = pos=(-2.84e-14,-74.9,43.1) rot=(0.57735,-0.57735,-0.57735;4.18879rad)
  Reference1 = -> Assembly [top.Edge3,top.Vertex3]
  Reference2 = -> Assembly [left_side.Edge6,left_side.Vertex1]
FEATURE [Sketcher::SketchObject] Sketch013
  ArcFitTolerance = 1e-06
  AttachmentSupport = -> [Pad006]
  ExternalGeometry = -> [Pad006]
  FullyConstrained = true
  MakeInternals = false
  MapMode = 5
  Placement = pos=(0,0,3.1) rot=(0,0,1;0rad)
  sketch-geometry (1):
    g0: Circle CenterX=0 CenterY=-35 CenterZ=0 NormalX=0 NormalY=0 NormalZ=1 AngleXU=0 Radius=30
  constraints (3):
    c: PointOnObject(g0,g-2)
    c: Diameter(g0) = 60
    c: Distance(g0,g-3) = 40
FEATURE [PartDesign::Pocket] Pocket006
  BaseFeature = -> Pad006
  Direction = (0,0,-1)
  Length = 1.55
  Length2 = 5
  Profile = -> Sketch013
  ReferenceAxis = -> Sketch013 [N_Axis]
  Refine = true
  Suppressed = false
  Type = 0
  expr: Length = <<dimensions>>.material_thickness / 2
FEATURE [Sketcher::SketchObject] Sketch014
  ArcFitTolerance = 1e-06
  AttachmentSupport = -> [Pocket006]
  ExternalGeometry = -> [Pocket006]
  FullyConstrained = true
  MakeInternals = false
  MapMode = 5
  Placement = pos=(0,0,1.55) rot=(0,0,1;0rad)
  sketch-geometry (1):
    g0: Circle CenterX=0 CenterY=-35 CenterZ=0 NormalX=0 NormalY=0 NormalZ=1 AngleXU=0 Radius=2.5
  constraints (2):
    c: Coincident(g0,g-3)
    c: Diameter(g0) = 5
FEATURE [PartDesign::Pocket] Pocket007
  BaseFeature = -> Pocket006
  Direction = (0,0,-1)
  Length = 5
  Length2 = 5
  Profile = -> Sketch014
  ReferenceAxis = -> Sketch014 [N_Axis]
  Refine = true
  Suppressed = false
  Type = 1
FEATURE [Sketcher::SketchObject] Sketch016
  ArcFitTolerance = 1e-06
  FullyConstrained = false
  MakeInternals = false
  MapMode = 5
  Placement = pos=(0,0,3.1) rot=(0,0,1;0rad)
  expr: Constraints[11] = <<dimensions>>.material_thickness + 3 mm
  expr: Constraints[36] = <<dimensions>>.material_thickness + 3 mm
  expr: Constraints[37] = <<dimensions>>.material_thickness
  expr: Constraints[42] = <<dimensions>>.material_thickness
  expr: Constraints[43] = <<dimensions>>.material_thickness
  expr: Constraints[44] = <<dimensions>>.material_thickness + 3 mm
  expr: Constraints[47] = <<dimensions>>.material_thickness + 3 mm
  expr: Constraints[8] = <<dimensions>>.material_thickness
  sketch-geometry (18):
    g0: LineSegment StartX=-36.1 StartY=-31.95 StartZ=0 EndX=-33 EndY=-31.95 EndZ=0
    g1: LineSegment StartX=-33 StartY=-31.95 StartZ=0 EndX=-33 EndY=-38.05 EndZ=0
    g2: LineSegment StartX=-33 StartY=-38.05 StartZ=0 EndX=-36.1 EndY=-38.05 EndZ=0
    g3: LineSegment StartX=-36.1 StartY=-38.05 StartZ=0 EndX=-36.1 EndY=-31.95 EndZ=0
    g4: LineSegment [constr] StartX=0 StartY=-35 StartZ=0 EndX=-63.8249 EndY=-35 EndZ=0
    g5: LineSegment [constr] StartX=0 StartY=-35 StartZ=0 EndX=57.2559 EndY=-35 EndZ=0
    g6: LineSegment StartX=-3.05 StartY=-2 StartZ=0 EndX=3.05 EndY=-2 EndZ=0
    g7: LineSegment StartX=3.05 StartY=-2 StartZ=0 EndX=3.05 EndY=1.1 EndZ=0
    g8: LineSegment StartX=3.05 StartY=1.1 StartZ=0 EndX=-3.05 EndY=1.1 EndZ=0
    g9: LineSegment StartX=-3.05 StartY=1.1 StartZ=0 EndX=-3.05 EndY=-2 EndZ=0
    g10: LineSegment StartX=33 StartY=-31.95 StartZ=0 EndX=33 EndY=-38.05 EndZ=0
    g11: LineSegment StartX=33 StartY=-38.05 StartZ=0 EndX=36.1 EndY=-38.05 EndZ=0
    g12: LineSegment StartX=36.1 StartY=-38.05 StartZ=0 EndX=36.1 EndY=-31.95 EndZ=0
    g13: LineSegment StartX=36.1 StartY=-31.95 StartZ=0 EndX=33 EndY=-31.95 EndZ=0
    g14: LineSegment StartX=-3.05 StartY=-68 StartZ=0 EndX=3.05 EndY=-68 EndZ=0
    g15: LineSegment StartX=3.05 StartY=-68 StartZ=0 EndX=3.05 EndY=-71.1 EndZ=0
    g16: LineSegment StartX=3.05 StartY=-71.1 StartZ=0 EndX=-3.05 EndY=-71.1 EndZ=0
    g17: LineSegment StartX=-3.05 StartY=-71.1 StartZ=0 EndX=-3.05 EndY=-68 EndZ=0
  constraints (48):
    c: Horizontal(g0)
    c: Coincident(g0,g1)
    c: Coincident(g1,g2)
    c: Coincident(g2,g3)
    c: Coincident(g3,g0)
    c: Vertical(g1)
    c: Horizontal(g2)
    c: Vertical(g3)
    c: DistanceX(g0,g0) = 3.1
    c: Coincident(g4,g-3)
    c: Symmetric(g0,g1,g4)
    c: DistanceY(g3,g3) = 6.1
    c: Coincident(g5,g4)
    c: Horizontal(g5)
    c: Distance(g-3,g1) = 3
    c: Coincident(g6,g7)
    c: Coincident(g7,g8)
    c: Coincident(g8,g9)
    c: Coincident(g9,g6)
    c: Coincident(g10,g11)
    c: Horizontal(g11)
    c: Coincident(g11,g12)
    c: Coincident(g12,g13)
    c: Coincident(g13,g10)
    c: Horizontal(g14)
    c: Coincident(g14,g15)
    c: Coincident(g15,g16)
    c: Coincident(g16,g17)
    c: Coincident(g17,g14)
    c: Vertical(g7)
    c: Vertical(g9)
    c: Horizontal(g6)
    c: Horizontal(g13)
    c: Vertical(g10)
    c: Vertical(g15)
    c: Vertical(g17)
    c: DistanceY(g12,g12) = 6.1
    c: DistanceX(g13,g13) = 3.1
    c: Symmetric(g12,g11,g5)
    c: Distance(g-3,g10) = 3
    c: Symmetric(g15,g16,g-2)
    c: Symmetric(g7,g8,g-2)
    c: Distance(g15,g15) = 3.1
    c: DistanceY(g7,g7) = 3.1
    c: DistanceX(g16,g16) = 6.1
    c: Distance(g-3,g14) = 3
    c: Distance(g-3,g6) = 3
    c: DistanceX(g8,g8) = 6.1
FEATURE [PartDesign::Pocket] Pocket008
  BaseFeature = -> Pocket007
  Direction = (0,0,-1)
  Length = 5
  Length2 = 5
  Profile = -> Sketch016
  ReferenceAxis = -> Sketch016 [N_Axis]
  Refine = true
  Suppressed = false
  Type = 1
FEATURE [Sketcher::SketchObject] Sketch017
  ArcFitTolerance = 1e-06
  AttachmentSupport = -> [XZ_Plane008]
  FullyConstrained = true
  MakeInternals = false
  MapMode = 5
  Placement = pos=(0,0,0) rot=(1,0,0;1.5708rad)
  expr: Constraints[19] = (<<dimensions>>.material_thickness + 3 mm) / 2 * 0.95
  sketch-geometry (8):
    g0: LineSegment StartX=0 StartY=5 StartZ=0 EndX=2.8975 EndY=5 EndZ=0
    g1: LineSegment StartX=2.8975 StartY=5 StartZ=0 EndX=2.8975 EndY=9.33 EndZ=0
    g2: LineSegment StartX=2.8975 StartY=9.33 StartZ=0 EndX=5 EndY=9.33 EndZ=0
    g3: LineSegment StartX=5 StartY=9.33 StartZ=0 EndX=5 EndY=45.67 EndZ=0
    g4: LineSegment StartX=5 StartY=45.67 StartZ=0 EndX=2.8975 EndY=45.67 EndZ=0
    g5: LineSegment StartX=2.8975 StartY=45.67 StartZ=0 EndX=2.8975 EndY=50 EndZ=0
    g6: LineSegment StartX=2.8975 StartY=50 StartZ=0 EndX=0 EndY=50 EndZ=0
    g7: LineSegment StartX=0 StartY=50 StartZ=0 EndX=0 EndY=5 EndZ=0
  constraints (24):
    c: PointOnObject(g0,g-2)
    c: Horizontal(g0)
    c: Coincident(g0,g1)
    c: Vertical(g1)
    c: Coincident(g1,g2)
    c: Horizontal(g2)
    c: Coincident(g2,g3)
    c: Vertical(g3)
    c: Coincident(g3,g4)
    c: Horizontal(g4)
    c: Coincident(g4,g5)
    c: Vertical(g5)
    c: Coincident(g5,g6)
    c: PointOnObject(g6,g-2)
    c: Coincident(g6,g7)
    c: Coincident(g7,g0)
    c: Horizontal(g6)
    c: Equal(g5,g1)
    c: DistanceY(g1,g1) = 4.33
    c: DistanceX(g0,g0) = 2.8975
    c: Equal(g6,g0)
    c: Distance(g6,g0) = 45
    c: Distance(g7,g3) = 5
    c: Distance(g0,g-1) = 5
FEATURE [PartDesign::Pad] Pad007
  Direction = (0,-1,2e-16)
  Length = 3.1
  Length2 = 10
  Placement = pos=(0,0,0) rot=(1,0,0;1.5708rad)
  Profile = -> Sketch017
  ReferenceAxis = -> Sketch017 [N_Axis]
  Refine = true
  Suppressed = false
  Type = 0
  expr: Length = <<dimensions>>.material_thickness
FEATURE [PartDesign::Mirrored] Mirrored001
  BaseFeature = -> Pad007
  MirrorPlane = -> Sketch017 [V_Axis]
  Originals = -> [Pad007]
  Placement = pos=(0,0,0) rot=(1,0,0;1.5708rad)
  Refine = true
  Suppressed = false
  TransformMode = 0
FEATURE [PartDesign::Body] Body007  label="cup_holder_vertical"
  AllowCompound = false
  Group = -> [Sketch017,Pad007,Mirrored001]
  Origin = -> Origin008
  Tip = -> Mirrored001
FEATURE [Sketcher::SketchObject] Sketch018
  ArcFitTolerance = 1e-06
  AttachmentSupport = -> [XY_Plane009]
  FullyConstrained = true
  MakeInternals = false
  MapMode = 5
  sketch-geometry (2):
    g0: Circle CenterX=0 CenterY=-35 CenterZ=0 NormalX=0 NormalY=0 NormalZ=1 AngleXU=0 Radius=10.5
    g1: Circle CenterX=0 CenterY=-35 CenterZ=0 NormalX=0 NormalY=0 NormalZ=1 AngleXU=0 Radius=15.5
  constraints (5):
    c: Diameter(g0) = 21
    c: PointOnObject(g0,g-2)
    c: Diameter(g1) = 31
    c: Coincident(g1,g0)
    c: Distance(g0,g-1) = 35
FEATURE [PartDesign::Pad] Pad008
  Direction = (0,0,1)
  Length = 3.1
  Length2 = 10
  Profile = -> Sketch018
  ReferenceAxis = -> Sketch018 [N_Axis]
  Refine = true
  Suppressed = false
  Type = 0
  expr: Length = <<dimensions>>.material_thickness
FEATURE [PartDesign::Body] Body008  label="support_ring"
  AllowCompound = false
  Group = -> [Sketch018,Pad008]
  Origin = -> Origin009
  Tip = -> Pad008
FEATURE [App::Link] cup_holder_vertical  label="cup_holder_vertical001"
  LinkPlacement = pos=(-4.73632,-34.95,113.153) rot=(0.425583,0.425583,0.798598;1.79382rad)
  LinkedObject = -> Body007
  Placement = pos=(-4.73632,-34.95,113.153) rot=(0.425583,0.425583,0.798598;1.79382rad)
FEATURE [App::Link] cup_holder_vertical001  label="cup_holder_vertical002"
  LinkPlacement = pos=(15.4223,-67.95,83.1458) rot=(0,1,0;0.979259rad)
  LinkedObject = -> Body007
  Placement = pos=(15.4223,-67.95,83.1458) rot=(0,1,0;0.979259rad)
FEATURE [App::Link] cup_holder_vertical002  label="cup_holder_vertical003"
  LinkPlacement = pos=(35.5251,-34.9,53.2213) rot=(-0.425583,0.425583,-0.798598;1.79382rad)
  LinkedObject = -> Body007
  Placement = pos=(35.5251,-34.9,53.2213) rot=(-0.425583,0.425583,-0.798598;1.79382rad)
FEATURE [App::Link] cup_holder_vertical003  label="cup_holder_vertical004"
  LinkPlacement = pos=(15.3944,1.15,83.1873) rot=(0,1,0;0.979259rad)
  LinkedObject = -> Body007
  Placement = pos=(15.3944,1.15,83.1873) rot=(0,1,0;0.979259rad)
FEATURE [App::Link] support_ring  label="support_ring001"
  LinkPlacement = pos=(0.0157366,0.51717,43.9206) rot=(0,0,1;0rad)
  LinkedObject = -> Body008
  Placement = pos=(0.0157366,0.51717,43.9206) rot=(0,0,1;0rad)
FEATURE [Sketcher::SketchObject] Sketch019
  ArcFitTolerance = 1e-06
  AttachmentSupport = -> [Pocket008]
  ExternalGeometry = -> [Pocket008]
  FullyConstrained = true
  MakeInternals = false
  MapMode = 5
  Placement = pos=(0,0,3.1) rot=(0,0,1;0rad)
  sketch-geometry (4):
    g0: LineSegment StartX=-35 StartY=58 StartZ=0 EndX=-35 EndY=13 EndZ=0
    g1: LineSegment StartX=-35 StartY=13 StartZ=0 EndX=35 EndY=13 EndZ=0
    g2: LineSegment StartX=35 StartY=13 StartZ=0 EndX=35 EndY=58 EndZ=0
    g3: LineSegment StartX=35 StartY=58 StartZ=0 EndX=-35 EndY=58 EndZ=0
  constraints (11):
    c: Vertical(g0)
    c: Coincident(g0,g1)
    c: Horizontal(g1)
    c: Coincident(g1,g2)
    c: Coincident(g2,g3)
    c: Coincident(g3,g0)
    c: Vertical(g2)
    c: Symmetric(g2,g0,g-2)
    c: DistanceX(g3,g3) = 70
    c: DistanceY(g2,g2) = 45
    c: Distance(g-3,g3) = 17
FEATURE [PartDesign::Pocket] Pocket009
  BaseFeature = -> Pocket008
  Direction = (0,0,-1)
  Length = 1.55
  Length2 = 5
  Profile = -> Sketch019
  ReferenceAxis = -> Sketch019 [N_Axis]
  Refine = true
  Suppressed = false
  Type = 0
  expr: Length = <<dimensions>>.material_thickness / 2
FEATURE [Sketcher::SketchObject] Sketch020
  ArcFitTolerance = 1e-06
  AttachmentSupport = -> [Pocket009]
  ExternalGeometry = -> [Pocket009]
  FullyConstrained = true
  MakeInternals = false
  MapMode = 5
  Placement = pos=(0,0,3.1) rot=(0,0,1;0rad)
  sketch-geometry (4):
    g0: ArcOfCircle CenterX=-65 CenterY=2 CenterZ=0 NormalX=0 NormalY=0 NormalZ=1 AngleXU=0 Radius=5 StartAngle=1.5708 EndAngle=4.71239
    g1: ArcOfCircle CenterX=-45 CenterY=2 CenterZ=0 NormalX=0 NormalY=0 NormalZ=1 AngleXU=0 Radius=5 StartAngle=4.71239 EndAngle=7.85398
    g2: LineSegment StartX=-65 StartY=7 StartZ=0 EndX=-45 EndY=7 EndZ=0
    g3: LineSegment StartX=-65 StartY=-3 StartZ=0 EndX=-45 EndY=-3 EndZ=0
  constraints (10):
    c: Tangent(g0,g2) = 1.5708
    c: Tangent(g0,g3) = -1.5708
    c: Tangent(g1,g2) = 1.5708
    c: Tangent(g1,g3) = -1.5708
    c: Equal(g0,g1)
    c: Horizontal(g2)
    c: Distance(g1,g-3) = 10
    c: Distance(g0,g-4) = 10
    c: Distance(g1,g-1) = 2
    c: Distance(g3,g2) = 10
FEATURE [PartDesign::Pocket] Pocket010
  BaseFeature = -> Pocket009
  Direction = (0,0,-1)
  Length = 5
  Length2 = 5
  Profile = -> Sketch020
  ReferenceAxis = -> Sketch020 [N_Axis]
  Refine = true
  Suppressed = false
  Type = 1
FEATURE [PartDesign::Body] Body006  label="top"
  AllowCompound = false
  Group = -> [Pad006,Sketch012,Sketch013,Pocket006,Sketch014,Pocket007,Sketch016,Pocket008,Sketch019,Pocket009,Sketch020,Pocket010]
  Origin = -> Origin007
  Tip = -> Pocket010
FEATURE [Part::Plane] Plane
  AttacherType = Attacher::AttachEngine3D
  Length = 170
  Placement = pos=(50,-90,-19) rot=(0,-1,0;1.5708rad)
  Width = 170
FEATURE [App::Part] Part
  Group = -> [Plane]
  Origin = -> Origin010
FEATURE [Sketcher::SketchObject] Sketch021
  ArcFitTolerance = 1e-06
  AttachmentSupport = -> [XY_Plane011]
  FullyConstrained = true
  MakeInternals = false
  MapMode = 5
  expr: Constraints[11] = <<dimensions>>.base_width
  expr: Constraints[12] = <<dimensions>>.base_length
  expr: Constraints[14] = <<dimensions>>.base_length / 2
  sketch-geometry (6):
    g0: LineSegment StartX=-75 StartY=50 StartZ=0 EndX=-75 EndY=-75 EndZ=0
    g1: LineSegment StartX=-75 StartY=-75 StartZ=0 EndX=75 EndY=-75 EndZ=0
    g2: LineSegment StartX=75 StartY=-75 StartZ=0 EndX=75 EndY=50 EndZ=0
    g3: LineSegment StartX=75 StartY=50 StartZ=0 EndX=50 EndY=75 EndZ=0
    g4: LineSegment StartX=50 StartY=75 StartZ=0 EndX=-50 EndY=75 EndZ=0
    g5: LineSegment StartX=-50 StartY=75 StartZ=0 EndX=-75 EndY=50 EndZ=0
  constraints (17):
    c: Vertical(g0)
    c: Coincident(g0,g1)
    c: Horizontal(g1)
    c: Coincident(g1,g2)
    c: Vertical(g2)
    c: Coincident(g2,g3)
    c: Coincident(g3,g4)
    c: Horizontal(g4)
    c: Coincident(g4,g5)
    c: Coincident(g5,g0)
    c: Equal(g5,g3)
    c: DistanceX(g1,g1) = 150
    c: Distance(g1,g4) = 150
    c: Symmetric(g0,g2,g-2)
    c: Distance(g-1,g1) = 75
    c: DistanceY(g0,g4) = 25
    c: DistanceX(g0,g4) = 25
FEATURE [PartDesign::Pad] Pad009
  Direction = (0,0,1)
  Length = 3.1
  Length2 = 10
  Profile = -> Sketch021
  ReferenceAxis = -> Sketch021 [N_Axis]
  Refine = true
  Suppressed = false
  Type = 0
  expr: Length = <<dimensions>>.material_thickness
FEATURE [Sketcher::SketchObject] Sketch022
  ArcFitTolerance = 1e-06
  AttachmentSupport = -> [Pad009]
  ExternalGeometry = -> [Pad009]
  FullyConstrained = true
  MakeInternals = false
  MapMode = 5
  Placement = pos=(0,0,3.1) rot=(0,0,1;0rad)
  sketch-geometry (1):
    g0: Circle CenterX=0 CenterY=-35 CenterZ=0 NormalX=0 NormalY=0 NormalZ=1 AngleXU=0 Radius=30
  constraints (3):
    c: PointOnObject(g0,g-2)
    c: Diameter(g0) = 60
    c: Distance(g0,g-3) = 40
FEATURE [PartDesign::Pocket] Pocket011
  BaseFeature = -> Pad009
  Direction = (0,0,-1)
  Length = 1.55
  Length2 = 5
  Profile = -> Sketch022
  ReferenceAxis = -> Sketch022 [N_Axis]
  Refine = true
  Suppressed = false
  Type = 0
  expr: Length = <<dimensions>>.material_thickness / 2
FEATURE [Sketcher::SketchObject] Sketch023
  ArcFitTolerance = 1e-06
  AttachmentSupport = -> [Pocket011]
  ExternalGeometry = -> [Pocket011]
  FullyConstrained = true
  MakeInternals = false
  MapMode = 5
  Placement = pos=(0,0,1.55) rot=(0,0,1;0rad)
  sketch-geometry (1):
    g0: Circle CenterX=0 CenterY=-35 CenterZ=0 NormalX=0 NormalY=0 NormalZ=1 AngleXU=0 Radius=2.5
  constraints (2):
    c: Coincident(g0,g-3)
    c: Diameter(g0) = 5
FEATURE [PartDesign::Pocket] Pocket012
  BaseFeature = -> Pocket011
  Direction = (0,0,-1)
  Length = 5
  Length2 = 5
  Profile = -> Sketch023
  ReferenceAxis = -> Sketch023 [N_Axis]
  Refine = true
  Suppressed = false
  Type = 1
FEATURE [Sketcher::SketchObject] Sketch024
  ArcFitTolerance = 1e-06
  FullyConstrained = false
  MakeInternals = false
  MapMode = 5
  Placement = pos=(0,0,3.1) rot=(0,0,1;0rad)
  expr: Constraints[11] = <<dimensions>>.material_thickness + 3 mm
  expr: Constraints[36] = <<dimensions>>.material_thickness + 3 mm
  expr: Constraints[37] = <<dimensions>>.material_thickness
  expr: Constraints[42] = <<dimensions>>.material_thickness
  expr: Constraints[43] = <<dimensions>>.material_thickness
  expr: Constraints[44] = <<dimensions>>.material_thickness + 3 mm
  expr: Constraints[47] = <<dimensions>>.material_thickness + 3 mm
  expr: Constraints[8] = <<dimensions>>.material_thickness
  sketch-geometry (18):
    g0: LineSegment StartX=-36.1 StartY=-31.95 StartZ=0 EndX=-33 EndY=-31.95 EndZ=0
    g1: LineSegment StartX=-33 StartY=-31.95 StartZ=0 EndX=-33 EndY=-38.05 EndZ=0
    g2: LineSegment StartX=-33 StartY=-38.05 StartZ=0 EndX=-36.1 EndY=-38.05 EndZ=0
    g3: LineSegment StartX=-36.1 StartY=-38.05 StartZ=0 EndX=-36.1 EndY=-31.95 EndZ=0
    g4: LineSegment [constr] StartX=0 StartY=-35 StartZ=0 EndX=-63.8249 EndY=-35 EndZ=0
    g5: LineSegment [constr] StartX=0 StartY=-35 StartZ=0 EndX=57.2559 EndY=-35 EndZ=0
    g6: LineSegment StartX=-3.05 StartY=-2 StartZ=0 EndX=3.05 EndY=-2 EndZ=0
    g7: LineSegment StartX=3.05 StartY=-2 StartZ=0 EndX=3.05 EndY=1.1 EndZ=0
    g8: LineSegment StartX=3.05 StartY=1.1 StartZ=0 EndX=-3.05 EndY=1.1 EndZ=0
    g9: LineSegment StartX=-3.05 StartY=1.1 StartZ=0 EndX=-3.05 EndY=-2 EndZ=0
    g10: LineSegment StartX=33 StartY=-31.95 StartZ=0 EndX=33 EndY=-38.05 EndZ=0
    g11: LineSegment StartX=33 StartY=-38.05 StartZ=0 EndX=36.1 EndY=-38.05 EndZ=0
    g12: LineSegment StartX=36.1 StartY=-38.05 StartZ=0 EndX=36.1 EndY=-31.95 EndZ=0
    g13: LineSegment StartX=36.1 StartY=-31.95 StartZ=0 EndX=33 EndY=-31.95 EndZ=0
    g14: LineSegment StartX=-3.05 StartY=-68 StartZ=0 EndX=3.05 EndY=-68 EndZ=0
    g15: LineSegment StartX=3.05 StartY=-68 StartZ=0 EndX=3.05 EndY=-71.1 EndZ=0
    g16: LineSegment StartX=3.05 StartY=-71.1 StartZ=0 EndX=-3.05 EndY=-71.1 EndZ=0
    g17: LineSegment StartX=-3.05 StartY=-71.1 StartZ=0 EndX=-3.05 EndY=-68 EndZ=0
  constraints (48):
    c: Horizontal(g0)
    c: Coincident(g0,g1)
    c: Coincident(g1,g2)
    c: Coincident(g2,g3)
    c: Coincident(g3,g0)
    c: Vertical(g1)
    c: Horizontal(g2)
    c: Vertical(g3)
    c: DistanceX(g0,g0) = 3.1
    c: Coincident(g4,g-3)
    c: Symmetric(g0,g1,g4)
    c: DistanceY(g3,g3) = 6.1
    c: Coincident(g5,g4)
    c: Horizontal(g5)
    c: Distance(g-3,g1) = 3
    c: Coincident(g6,g7)
    c: Coincident(g7,g8)
    c: Coincident(g8,g9)
    c: Coincident(g9,g6)
    c: Coincident(g10,g11)
    c: Horizontal(g11)
    c: Coincident(g11,g12)
    c: Coincident(g12,g13)
    c: Coincident(g13,g10)
    c: Horizontal(g14)
    c: Coincident(g14,g15)
    c: Coincident(g15,g16)
    c: Coincident(g16,g17)
    c: Coincident(g17,g14)
    c: Vertical(g7)
    c: Vertical(g9)
    c: Horizontal(g6)
    c: Horizontal(g13)
    c: Vertical(g10)
    c: Vertical(g15)
    c: Vertical(g17)
    c: DistanceY(g12,g12) = 6.1
    c: DistanceX(g13,g13) = 3.1
    c: Symmetric(g12,g11,g5)
    c: Distance(g-3,g10) = 3
    c: Symmetric(g15,g16,g-2)
    c: Symmetric(g7,g8,g-2)
    c: Distance(g15,g15) = 3.1
    c: DistanceY(g7,g7) = 3.1
    c: DistanceX(g16,g16) = 6.1
    c: Distance(g-3,g14) = 3
    c: Distance(g-3,g6) = 3
    c: DistanceX(g8,g8) = 6.1
FEATURE [PartDesign::Pocket] Pocket013
  BaseFeature = -> Pocket012
  Direction = (0,0,-1)
  Length = 5
  Length2 = 5
  Profile = -> Sketch024
  ReferenceAxis = -> Sketch024 [N_Axis]
  Refine = true
  Suppressed = false
  Type = 1
FEATURE [Sketcher::SketchObject] Sketch025
  ArcFitTolerance = 1e-06
  AttachmentSupport = -> [Pocket013]
  ExternalGeometry = -> [Pocket013]
  FullyConstrained = true
  MakeInternals = false
  MapMode = 5
  Placement = pos=(0,0,3.1) rot=(0,0,1;0rad)
  sketch-geometry (4):
    g0: LineSegment StartX=-35 StartY=58 StartZ=0 EndX=-35 EndY=13 EndZ=0
    g1: LineSegment StartX=-35 StartY=13 StartZ=0 EndX=35 EndY=13 EndZ=0
    g2: LineSegment StartX=35 StartY=13 StartZ=0 EndX=35 EndY=58 EndZ=0
    g3: LineSegment StartX=35 StartY=58 StartZ=0 EndX=-35 EndY=58 EndZ=0
  constraints (11):
    c: Vertical(g0)
    c: Coincident(g0,g1)
    c: Horizontal(g1)
    c: Coincident(g1,g2)
    c: Coincident(g2,g3)
    c: Coincident(g3,g0)
    c: Vertical(g2)
    c: Symmetric(g2,g0,g-2)
    c: DistanceX(g3,g3) = 70
    c: DistanceY(g2,g2) = 45
    c: Distance(g-3,g3) = 17
FEATURE [PartDesign::Pocket] Pocket014
  BaseFeature = -> Pocket013
  Direction = (0,0,-1)
  Length = 1.55
  Length2 = 5
  Profile = -> Sketch025
  ReferenceAxis = -> Sketch025 [N_Axis]
  Refine = true
  Suppressed = false
  Type = 0
  expr: Length = <<dimensions>>.material_thickness / 2
FEATURE [Sketcher::SketchObject] Sketch026
  ArcFitTolerance = 1e-06
  AttachmentSupport = -> [Pocket014]
  ExternalGeometry = -> [Pocket014]
  FullyConstrained = true
  MakeInternals = false
  MapMode = 5
  Placement = pos=(0,0,3.1) rot=(0,0,1;0rad)
  sketch-geometry (4):
    g0: ArcOfCircle CenterX=-65 CenterY=2 CenterZ=0 NormalX=0 NormalY=0 NormalZ=1 AngleXU=0 Radius=5 StartAngle=1.5708 EndAngle=4.71239
    g1: ArcOfCircle CenterX=-45 CenterY=2 CenterZ=0 NormalX=0 NormalY=0 NormalZ=1 AngleXU=0 Radius=5 StartAngle=4.71239 EndAngle=7.85398
    g2: LineSegment StartX=-65 StartY=7 StartZ=0 EndX=-45 EndY=7 EndZ=0
    g3: LineSegment StartX=-65 StartY=-3 StartZ=0 EndX=-45 EndY=-3 EndZ=0
  constraints (10):
    c: Tangent(g0,g2) = 1.5708
    c: Tangent(g0,g3) = -1.5708
    c: Tangent(g1,g2) = 1.5708
    c: Tangent(g1,g3) = -1.5708
    c: Equal(g0,g1)
    c: Horizontal(g2)
    c: Distance(g1,g-3) = 10
    c: Distance(g0,g-4) = 10
    c: Distance(g1,g-1) = 2
    c: Distance(g3,g2) = 10
FEATURE [PartDesign::Pocket] Pocket015
  BaseFeature = -> Pocket014
  Direction = (0,0,-1)
  Length = 5
  Length2 = 5
  Profile = -> Sketch026
  ReferenceAxis = -> Sketch026 [N_Axis]
  Refine = true
  Suppressed = false
  Type = 1
FEATURE [PartDesign::Body] Body009  label="top_copy"
  AllowCompound = false
  Group = -> [Pad009,Sketch021,Sketch022,Pocket011,Sketch023,Pocket012,Sketch024,Pocket013,Sketch025,Pocket014,Sketch026,Pocket015]
  Origin = -> Origin011
  Tip = -> Pocket015
FEATURE [Part::FeaturePython] Slice  # WARN: FeaturePython — macro-defined, semantics opaque (R4)
  Base = -> Body009
  Mode = 1
  Tolerance = 0
  Tools = -> [Plane]
FEATURE [Part::FeaturePython] Slice_child0  label="Slice.0"  # WARN: FeaturePython — macro-defined, semantics opaque (R4)
  Base = -> Slice
  FilterType = 1
  Invert = false
  OverrideMaxVal = 0
  WindowFrom = 80
  WindowTo = 100
  items = 0
FEATURE [Part::FeaturePython] Slice_child1  label="Slice.1"  # WARN: FeaturePython — macro-defined, semantics opaque (R4)
  Base = -> Slice
  FilterType = 1
  Invert = false
  OverrideMaxVal = 0
  WindowFrom = 80
  WindowTo = 100
  items = 1
FEATURE [App::DocumentObjectGroup] GrExplode_Slice  label="Exploded Slice"
  Group = -> [Slice_child0,Slice_child1]
FEATURE [App::Link] Slice_1  label="Slice.002"
  LinkPlacement = pos=(-2.84e-14,0.05,43.1) rot=(0,0,1;0rad)
  LinkedObject = -> Slice_child1
  Placement = pos=(-2.84e-14,0.05,43.1) rot=(0,0,1;0rad)
FEATURE [App::Link] Slice_0  label="Slice.003"
  LinkPlacement = pos=(19.5448,0.05,85.9755) rot=(0,1,0;0.979259rad)
  LinkedObject = -> Slice_child0
  Placement = pos=(19.5448,0.05,85.9755) rot=(0,1,0;0.979259rad)
FEATURE [App::FeaturePython] Joint015  label="Fixed012"  # Assembly joint (typed FeaturePython)
  Activated = true
  AngleMax = 0
  AngleMin = 0
  Detach1 = false
  Detach2 = false
  Distance = 0
  Distance2 = 0
  EnableAngleMax = false
  EnableAngleMin = false
  EnableLengthMax = false
  EnableLengthMin = false
  JointType = 0 (Fixed)
  LengthMax = 0
  LengthMin = 0
  Offset2 = pos=(0,0,-1) rot=(0,0,1;0rad)
  Placement1 = pos=(75,-12.5,0) rot=(0.57735,0.57735,0.57735;4.18879rad)
  Placement2 = pos=(3.1,-12.45,43.1) rot=(0.57735,0.57735,0.57735;4.18879rad)
  Reference1 = -> Assembly [Slice_1.Edge7,Slice_1.Edge7]
  Reference2 = -> Assembly [right_side.Edge12,right_side.Edge12]
FEATURE [App::FeaturePython] Joint016  label="Revolute"  # Assembly joint (typed FeaturePython)
  Activated = true
  AngleMax = 90
  AngleMin = 0
  Detach1 = false
  Detach2 = false
  Distance = 0
  Distance2 = 0
  EnableAngleMax = true
  EnableAngleMin = true
  EnableLengthMax = false
  EnableLengthMin = false
  JointType = 1 (Revolute)
  LengthMax = 0
  LengthMin = 0
  Placement1 = pos=(50,-1.02e-14,3.1) rot=(-0.57735,-0.57735,0.57735;4.18879rad)
  Placement2 = pos=(50,-1.07e-14,3.1) rot=(-0.57735,-0.57735,0.57735;4.18879rad)
  Reference1 = -> Assembly [Slice_0.Edge35,Slice_0.Edge35]
  Reference2 = -> Assembly [Slice_1.Edge10,Slice_1.Edge10]
FEATURE [Sketcher::SketchObject] Sketch027
  ArcFitTolerance = 1e-06
  AttachmentSupport = -> [YZ_Plane012]
  FullyConstrained = false
  MakeInternals = false
  MapMode = 5
  Placement = pos=(0,0,0) rot=(0.57735,0.57735,0.57735;2.0944rad)
  sketch-geometry (3):
    g0: LineSegment StartX=-41.1568 StartY=57.5256 StartZ=0 EndX=-41.1568 EndY=37.5256 EndZ=0
    g1: LineSegment StartX=-41.1568 StartY=37.5256 StartZ=0 EndX=-21.1568 EndY=37.5256 EndZ=0
    g2: ArcOfCircle CenterX=-13.6602 CenterY=65.0223 CenterZ=0 NormalX=0 NormalY=0 NormalZ=1 AngleXU=0 Radius=28.5003 StartAngle=3.40776 EndAngle=4.44622
  constraints (7):
    c: Vertical(g0)
    c: Coincident(g0,g1)
    c: DistanceX(g1,g1) = 20
    c: Equal(g0,g1)
    c: Horizontal(g1)
    c: Coincident(g2,g0)
    c: Coincident(g2,g1)
FEATURE [PartDesign::Pad] Pad010
  Direction = (1,0,0)
  Length = 3.1
  Length2 = 10
  Placement = pos=(0,0,0) rot=(1,1,1;2.0944rad)
  Profile = -> Sketch027
  ReferenceAxis = -> Sketch027 [N_Axis]
  Refine = true
  Suppressed = false
  Type = 0
  expr: Length = <<dimensions>>.material_thickness
FEATURE [PartDesign::Body] Body010  label="support"
  AllowCompound = false
  Group = -> [Sketch027,Pad010]
  Origin = -> Origin012
  Tip = -> Pad010
FEATURE [Sketcher::SketchObject] Sketch028
  ArcFitTolerance = 1e-06
  AttachmentSupport = -> [Pocket003]
  ExternalGeometry = -> [Pocket003]
  FullyConstrained = true
  MakeInternals = false
  MapMode = 5
  Placement = pos=(0,0,3.1) rot=(0,0,1;0rad)
  expr: Constraints[10] = <<dimensions>>.material_thickness + <<dimensions>>.hole_margin
  sketch-geometry (4):
    g0: LineSegment StartX=28.1 StartY=-5.11249 StartZ=0 EndX=28.1 EndY=-53.9 EndZ=0
    g1: LineSegment StartX=28.1 StartY=-53.9 StartZ=0 EndX=70.9 EndY=-53.9 EndZ=0
    g2: LineSegment StartX=70.9 StartY=-53.9 StartZ=0 EndX=70.9 EndY=-5.11249 EndZ=0
    g3: LineSegment StartX=70.9 StartY=-5.11249 StartZ=0 EndX=28.1 EndY=-5.11249 EndZ=0
  constraints (12):
    c: Vertical(g0)
    c: Coincident(g0,g1)
    c: Horizontal(g1)
    c: Coincident(g1,g2)
    c: Coincident(g2,g3)
    c: Coincident(g3,g0)
    c: Horizontal(g3)
    c: Distance(g-4,g1) = 8
    c: Vertical(g2)
    c: Distance(g3,g-7) = 7
    c: Distance(g-6,g2) = 4.1
    c: Distance(g-5,g0) = 10
FEATURE [PartDesign::Pocket] Pocket016
  BaseFeature = -> Pocket003
  Direction = (0,0,-1)
  Length = 1.55
  Length2 = 5
  Profile = -> Sketch028
  ReferenceAxis = -> Sketch028 [N_Axis]
  Refine = true
  Suppressed = false
  Type = 0
  expr: Length = <<dimensions>>.material_thickness / 2
FEATURE [PartDesign::Body] Body  label="base"
  AllowCompound = false
  Group = -> [Sketch,Pad,Sketch001,Pocket,Sketch002,Pocket001,Sketch003,Pocket002,Fillet,Sketch004,Pocket003,Sketch028,Pocket016]
  Origin = -> Origin
  Tip = -> Pocket016
FEATURE [App::FeaturePython] Joint017  label="Fixed013"  # Assembly joint (typed FeaturePython)
  Activated = true
  AngleMax = 0
  AngleMin = 0
  Detach1 = false
  Detach2 = false
  Distance = 0
  Distance2 = 0
  EnableAngleMax = false
  EnableAngleMin = false
  EnableLengthMax = false
  EnableLengthMin = false
  JointType = 0 (Fixed)
  LengthMax = 0
  LengthMin = 0
  Placement1 = pos=(-7.1e-15,-3.1,5) rot=(0.707107,0,0.707107;3.14159rad)
  Placement2 = pos=(0,-2,0) rot=(0.707107,0,0.707107;3.14159rad)
  Reference1 = -> Assembly [cup_holder_vertical003.Edge17,cup_holder_vertical003.Edge17]
  Reference2 = -> Assembly [Slice_0.Edge30,Slice_0.Edge30]
FEATURE [App::FeaturePython] Joint018  label="Fixed014"  # Assembly joint (typed FeaturePython)
  Activated = true
  AngleMax = 0
  AngleMin = 0
  Detach1 = false
  Detach2 = false
  Distance = 0
  Distance2 = 0
  EnableAngleMax = false
  EnableAngleMin = false
  EnableLengthMax = false
  EnableLengthMin = false
  JointType = 0 (Fixed)
  LengthMax = 0
  LengthMin = 0
  Offset2 = pos=(0,0,0) rot=(0,0,1;3.14159rad)
  Placement1 = pos=(0,-3.1,5) rot=(0.707107,0,0.707107;3.14159rad)
  Placement2 = pos=(-33,-35,0) rot=(-0.57735,0.57735,-0.57735;4.18879rad)
  Reference1 = -> Assembly [cup_holder_vertical.Edge17,cup_holder_vertical.Edge17]
  Reference2 = -> Assembly [Slice_0.Edge16,Slice_0.Edge16]
FEATURE [App::FeaturePython] Joint019  label="Fixed015"  # Assembly joint (typed FeaturePython)
  Activated = true
  AngleMax = 0
  AngleMin = 0
  Detach1 = false
  Detach2 = false
  Distance = 0
  Distance2 = 0
  EnableAngleMax = false
  EnableAngleMin = false
  EnableLengthMax = false
  EnableLengthMin = false
  JointType = 0 (Fixed)
  LengthMax = 0
  LengthMin = 0
  Offset2 = pos=(0,0,3) rot=(0,0,1;3.14159rad)
  Placement1 = pos=(-1.42e-14,-3.1,5) rot=(0.707107,0,0.707107;3.14159rad)
  Placement2 = pos=(0.05,-71.1,-3e-10) rot=(0,-1,0;1.5708rad)
  Reference1 = -> Assembly [cup_holder_vertical001.Edge17,cup_holder_vertical001.Edge17]
  Reference2 = -> Assembly [Slice_0.Edge18,Slice_0.Vertex16]
FEATURE [App::FeaturePython] Joint020  label="Fixed016"  # Assembly joint (typed FeaturePython)
  Activated = true
  AngleMax = 0
  AngleMin = 0
  Detach1 = false
  Detach2 = false
  Distance = 0
  Distance2 = 0
  EnableAngleMax = false
  EnableAngleMin = false
  EnableLengthMax = false
  EnableLengthMin = false
  JointType = 0 (Fixed)
  LengthMax = 0
  LengthMin = 0
  Offset2 = pos=(0,0,3) rot=(0,0,1;3.14159rad)
  Placement1 = pos=(0,-3.1,5) rot=(0.707107,0,0.707107;3.14159rad)
  Placement2 = pos=(33,-34.95,0) rot=(-0.57735,0.57735,-0.57735;4.18879rad)
  Reference1 = -> Assembly [cup_holder_vertical002.Edge17,cup_holder_vertical002.Edge17]
  Reference2 = -> Assembly [Slice_0.Edge22,Slice_0.Vertex19]
FEATURE [Sketcher::SketchObject] Sketch029
  ArcFitTolerance = 1e-06
  AttachmentSupport = -> [XY_Plane013]
  FullyConstrained = false
  MakeInternals = false
  MapMode = 5
  expr: Constraints[13] = <<dimensions>>.material_thickness
  expr: Constraints[14] = <<dimensions>>.material_thickness + 3 mm
  expr: Constraints[36] = <<dimensions>>.material_thickness + 3 mm
  expr: Constraints[37] = <<dimensions>>.material_thickness
  sketch-geometry (20):
    g0: Circle CenterX=0 CenterY=-35 CenterZ=0 NormalX=0 NormalY=0 NormalZ=1 AngleXU=0 Radius=30.5
    g1: Circle CenterX=0 CenterY=-35 CenterZ=0 NormalX=0 NormalY=0 NormalZ=1 AngleXU=0 Radius=38.5
    g2: LineSegment StartX=-35.6 StartY=-31.95 StartZ=0 EndX=-35.6 EndY=-38.05 EndZ=0
    g3: LineSegment StartX=-35.6 StartY=-38.05 StartZ=0 EndX=-32.5 EndY=-38.05 EndZ=0
    g4: LineSegment StartX=-32.5 StartY=-38.05 StartZ=0 EndX=-32.5 EndY=-31.95 EndZ=0
    g5: LineSegment StartX=-32.5 StartY=-31.95 StartZ=0 EndX=-35.6 EndY=-31.95 EndZ=0
    g6: LineSegment [constr] StartX=0 StartY=-35 StartZ=0 EndX=-58.4868 EndY=-35 EndZ=0
    g7: LineSegment [constr] StartX=0 StartY=-35 StartZ=0 EndX=54.8346 EndY=-35 EndZ=0
    g8: LineSegment StartX=32.5 StartY=-31.95 StartZ=0 EndX=32.5 EndY=-38.05 EndZ=0
    g9: LineSegment StartX=32.5 StartY=-38.05 StartZ=0 EndX=35.6 EndY=-38.05 EndZ=0
    g10: LineSegment StartX=35.6 StartY=-38.05 StartZ=0 EndX=35.6 EndY=-31.95 EndZ=0
    g11: LineSegment StartX=35.6 StartY=-31.95 StartZ=0 EndX=32.5 EndY=-31.95 EndZ=0
    g12: LineSegment StartX=-3.05 StartY=0.6 StartZ=0 EndX=-3.05 EndY=-2.5 EndZ=0
    g13: LineSegment StartX=-3.05 StartY=-2.5 StartZ=0 EndX=3.05 EndY=-2.5 EndZ=0
    g14: LineSegment StartX=3.05 StartY=-2.5 StartZ=0 EndX=3.05 EndY=0.6 EndZ=0
    g15: LineSegment StartX=3.05 StartY=0.6 StartZ=0 EndX=-3.05 EndY=0.6 EndZ=0
    g16: LineSegment StartX=-3.05 StartY=-67.5 StartZ=0 EndX=-3.05 EndY=-70.6 EndZ=0
    g17: LineSegment StartX=-3.05 StartY=-70.6 StartZ=0 EndX=3.05 EndY=-70.6 EndZ=0
    g18: LineSegment StartX=3.05 StartY=-70.6 StartZ=0 EndX=3.05 EndY=-67.5 EndZ=0
    g19: LineSegment StartX=3.05 StartY=-67.5 StartZ=0 EndX=-3.05 EndY=-67.5 EndZ=0
  constraints (49):
    c: Diameter(g0) = 61
    c: PointOnObject(g0,g-2)
    c: Coincident(g1,g0)
    c: Distance(g0,g1) = 8
    c: Distance(g0,g-1) = 35
    c: Coincident(g2,g3)
    c: Coincident(g3,g4)
    c: Coincident(g4,g5)
    c: Coincident(g5,g2)
    c: Vertical(g2)
    c: Vertical(g4)
    c: Horizontal(g3)
    c: Horizontal(g5)
    c: DistanceX(g5,g5) = 3.1
    c: DistanceY(g2,g2) = 6.1
    c: Distance(g0,g4) = 2
    c: Coincident(g6,g0)
    c: Coincident(g7,g0)
    c: Horizontal(g7)
    c: Symmetric(g4,g3,g6)
    c: Coincident(g8,g9)
    c: Coincident(g9,g10)
    c: Coincident(g10,g11)
    c: Coincident(g11,g8)
    c: Vertical(g10)
    c: Horizontal(g11)
    c: Symmetric(g4,g8,g0)
    c: Symmetric(g3,g8,g0)
    c: Symmetric(g2,g9,g0)
    c: Coincident(g12,g13)
    c: Coincident(g13,g14)
    c: Coincident(g14,g15)
    c: Coincident(g15,g12)
    c: Vertical(g12)
    c: Vertical(g14)
    c: Horizontal(g13)
    c: DistanceX(g13,g13) = 6.1
    c: DistanceY(g14,g14) = 3.1
    c: Distance(g0,g13) = 2
    c: Symmetric(g12,g14,g-2)
    c: Coincident(g16,g17)
    c: Coincident(g17,g18)
    c: Coincident(g18,g19)
    c: Coincident(g19,g16)
    c: Vertical(g16)
    c: Horizontal(g17)
    c: Symmetric(g12,g18,g0)
    c: Symmetric(g13,g16,g0)
    c: Symmetric(g12,g17,g0)
FEATURE [PartDesign::Pad] Pad011
  Direction = (0,0,1)
  Length = 3.1
  Length2 = 10
  Profile = -> Sketch029
  ReferenceAxis = -> Sketch029 [N_Axis]
  Refine = true
  Suppressed = false
  Type = 0
  expr: Length = <<dimensions>>.material_thickness
FEATURE [PartDesign::Body] Body011  label="cup_holder_top"
  AllowCompound = false
  Group = -> [Sketch029,Pad011]
  Origin = -> Origin013
  Tip = -> Pad011
FEATURE [App::Link] cup_holder_top  label="cup_holder_top001"
  LinkPlacement = pos=(54.0465,0.05,109.756) rot=(0,1,0;0.979259rad)
  LinkedObject = -> Body011
  Placement = pos=(54.0465,0.05,109.756) rot=(0,1,0;0.979259rad)
FEATURE [App::FeaturePython] Joint021  label="Fixed017"  # Assembly joint (typed FeaturePython)
  Activated = true
  AngleMax = 0
  AngleMin = 0
  Detach1 = false
  Detach2 = false
  Distance = 0
  Distance2 = 0
  EnableAngleMax = false
  EnableAngleMin = false
  EnableLengthMax = false
  EnableLengthMin = false
  JointType = 0 (Fixed)
  LengthMax = 0
  LengthMin = 0
  Offset2 = pos=(0,0,0) rot=(0,0,1;3.14159rad)
  Placement1 = pos=(-35.6,-35,3.1) rot=(-0.57735,-0.57735,0.57735;4.18879rad)
  Placement2 = pos=(7.1e-15,0,50) rot=(0,-1,0;4.71239rad)
  Reference1 = -> Assembly [cup_holder_top.Edge46,cup_holder_top.Edge46]
  Reference2 = -> Assembly [cup_holder_vertical.Edge35,cup_holder_vertical.Edge35]
FEATURE [Assembly::JointGroup] Joints
  Group = -> [GroundedJoint,Joint,Joint001,Joint002,Joint003,Joint004,Joint005,Joint007,Joint015,Joint016,Joint017,Joint018,Joint019,Joint020,Joint021]
FEATURE [Assembly::AssemblyObject] Assembly
  Group = -> [Joints,base,GroundedJoint,back_side,Joint,left_side,right_side,Joint001,Joint002,front_angle_side,front_angle_side001,Joint003,Joint004,front_side,Joint005,Joint007,cup_holder_vertical,cup_holder_vertical001,cup_holder_vertical002,cup_holder_vertical003,support_ring,Slice_1,Slice_0,Joint015,Joint016,Joint017,Joint018,Joint019,Joint020,cup_holder_top,Joint021]
  Origin = -> Origin006
  Type = Assembly
FEATURE [Part::Part2DObjectPython] Shape2DView  label="base_lines"  # Draft 2D object (typed FeaturePython)
  AutoUpdate = true
  Base = -> Body
  Clip = false
  FuseArch = false
  HiddenLines = false
  InPlace = true
  OnlySolids = false
  Projection = (0,0,1)
  ProjectionMode = 0
  SegmentLength = 0.05
  Tessellation = false
  VisibleOnly = false
FEATURE [Part::Part2DObjectPython] Shape2DView001  label="back_side_lines"  # Draft 2D object (typed FeaturePython)
  AutoUpdate = true
  Base = -> Body001
  Clip = false
  FuseArch = false
  HiddenLines = false
  InPlace = true
  OnlySolids = false
  Projection = (0,-1,0)
  ProjectionMode = 0
  SegmentLength = 0.05
  Tessellation = false
  VisibleOnly = false
FEATURE [Part::Part2DObjectPython] Shape2DView002  label="right_side_lines"  # Draft 2D object (typed FeaturePython)
  AutoUpdate = true
  Base = -> Pad002
  Clip = false
  FaceNumbers = [4]
  FuseArch = false
  HiddenLines = false
  InPlace = true
  OnlySolids = false
  Projection = (-1,0,0)
  ProjectionMode = 0
  SegmentLength = 0.05
  Tessellation = false
  VisibleOnly = false
FEATURE [Part::Part2DObjectPython] Shape2DView003  label="left_side_lines"  # Draft 2D object (typed FeaturePython)
  AutoUpdate = true
  Base = -> Pocket005
  Clip = false
  FaceNumbers = [3]
  FuseArch = false
  HiddenLines = false
  InPlace = true
  OnlySolids = false
  Projection = (-1,0,0)
  ProjectionMode = 0
  SegmentLength = 0.05
  Tessellation = false
  VisibleOnly = false
FEATURE [Part::Part2DObjectPython] Shape2DView004  label="front_angle_lines"  # Draft 2D object (typed FeaturePython)
  AutoUpdate = true
  Base = -> Pad004
  Clip = false
  FuseArch = false
  HiddenLines = false
  InPlace = true
  OnlySolids = false
  Projection = (0,1,0)
  ProjectionMode = 0
  SegmentLength = 0.05
  Tessellation = false
  VisibleOnly = false
FEATURE [Part::Part2DObjectPython] Shape2DView005  label="front_side_lines"  # Draft 2D object (typed FeaturePython)
  AutoUpdate = true
  Base = -> Mirrored
  Clip = false
  FaceNumbers = [6]
  FuseArch = false
  HiddenLines = false
  InPlace = true
  OnlySolids = false
  Projection = (0,-1,0)
  ProjectionMode = 0
  SegmentLength = 0.05
  Tessellation = false
  VisibleOnly = false
FEATURE [Part::Part2DObjectPython] Shape2DView006  label="support_ring_lines"  # Draft 2D object (typed FeaturePython)
  AutoUpdate = true
  Base = -> Pad008
  Clip = false
  FuseArch = false
  HiddenLines = false
  InPlace = true
  OnlySolids = false
  Projection = (-0.0117058,-0.0294219,0.999499)
  ProjectionMode = 0
  SegmentLength = 0.05
  Tessellation = false
  VisibleOnly = false
FEATURE [Part::Part2DObjectPython] Shape2DView007  label="vertical_cupholder_lines"  # Draft 2D object (typed FeaturePython)
  AutoUpdate = true
  Base = -> Mirrored001
  Clip = false
  FaceNumbers = [12]
  FuseArch = false
  HiddenLines = false
  InPlace = true
  OnlySolids = false
  Projection = (0,-1,0)
  ProjectionMode = 0
  SegmentLength = 0.05
  Tessellation = false
  VisibleOnly = false
FEATURE [Part::Part2DObjectPython] Shape2DView008  label="top_left_lines"  # Draft 2D object (typed FeaturePython)
  AutoUpdate = true
  Base = -> Slice_child0
  Clip = false
  FuseArch = false
  HiddenLines = false
  InPlace = true
  OnlySolids = false
  Projection = (-0.101173,-0.0218673,0.994628)
  ProjectionMode = 0
  SegmentLength = 0.05
  Tessellation = false
  VisibleOnly = false
FEATURE [Part::Part2DObjectPython] Shape2DView009  label="top_right_lines"  # Draft 2D object (typed FeaturePython)
  AutoUpdate = true
  Base = -> Slice_child1
  Clip = false
  FaceNumbers = [3]
  FuseArch = false
  HiddenLines = false
  InPlace = true
  OnlySolids = false
  Projection = (-0.101173,-0.0218673,0.994628)
  ProjectionMode = 0
  SegmentLength = 0.05
  Tessellation = false
  VisibleOnly = false
FEATURE [Part::Part2DObjectPython] Shape2DView010  label="support_arc_lines"  # Draft 2D object (typed FeaturePython)
  AutoUpdate = true
  Base = -> Pad010
  Clip = false
  FuseArch = false
  HiddenLines = false
  InPlace = true
  OnlySolids = false
  Projection = (-1,0,0)
  ProjectionMode = 0
  SegmentLength = 0.05
  Tessellation = false
  VisibleOnly = false
FEATURE [Part::Part2DObjectPython] Shape2DView011  label="cupholder_lines"  # Draft 2D object (typed FeaturePython)
  AutoUpdate = true
  Base = -> Pad011
  Clip = false
  FuseArch = false
  HiddenLines = false
  InPlace = true
  OnlySolids = false
  Projection = (0,0,1)
  ProjectionMode = 0
  SegmentLength = 0.05
  Tessellation = false
  VisibleOnly = false
FEATURE [App::DocumentObjectGroup] Group  label="Lines"
  Group = -> [Shape2DView,Shape2DView001,Shape2DView002,Shape2DView003,Shape2DView004,Shape2DView005,Shape2DView006,Shape2DView007,Shape2DView008,Shape2DView009,Shape2DView010,Shape2DView011]
